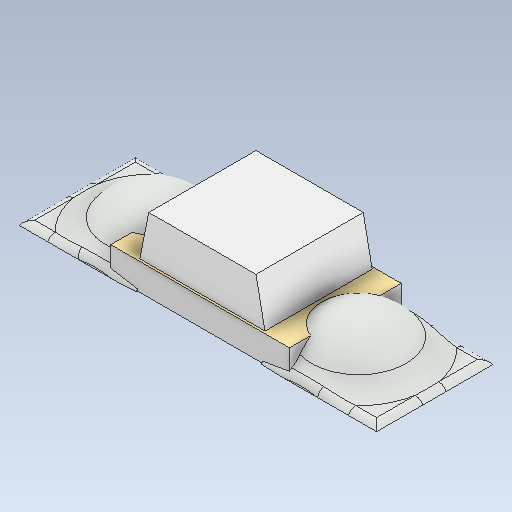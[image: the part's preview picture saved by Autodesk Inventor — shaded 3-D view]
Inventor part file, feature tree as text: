
AUTODESK INVENTOR PART (.ipt)
format: ipt  version: 2020 (Build 240168000, 168)  size: 219,648 bytes
history: native  units: in
note: dims shown in document units (in); Inventor stores cm internally (conversion verified against a paired STEP export)
features: mirror x1, other x1
ambient origin geometry x8: Origin, YZ Plane, XZ Plane, XY Plane, X Axis, Y Axis, Z Axis, Center Point
bodies: Solid1 (feature_tree), Solid2 (feature_tree)
feature tree (2):
  mirror  "Mirror3"
  other  "Boss-Extrude5"
